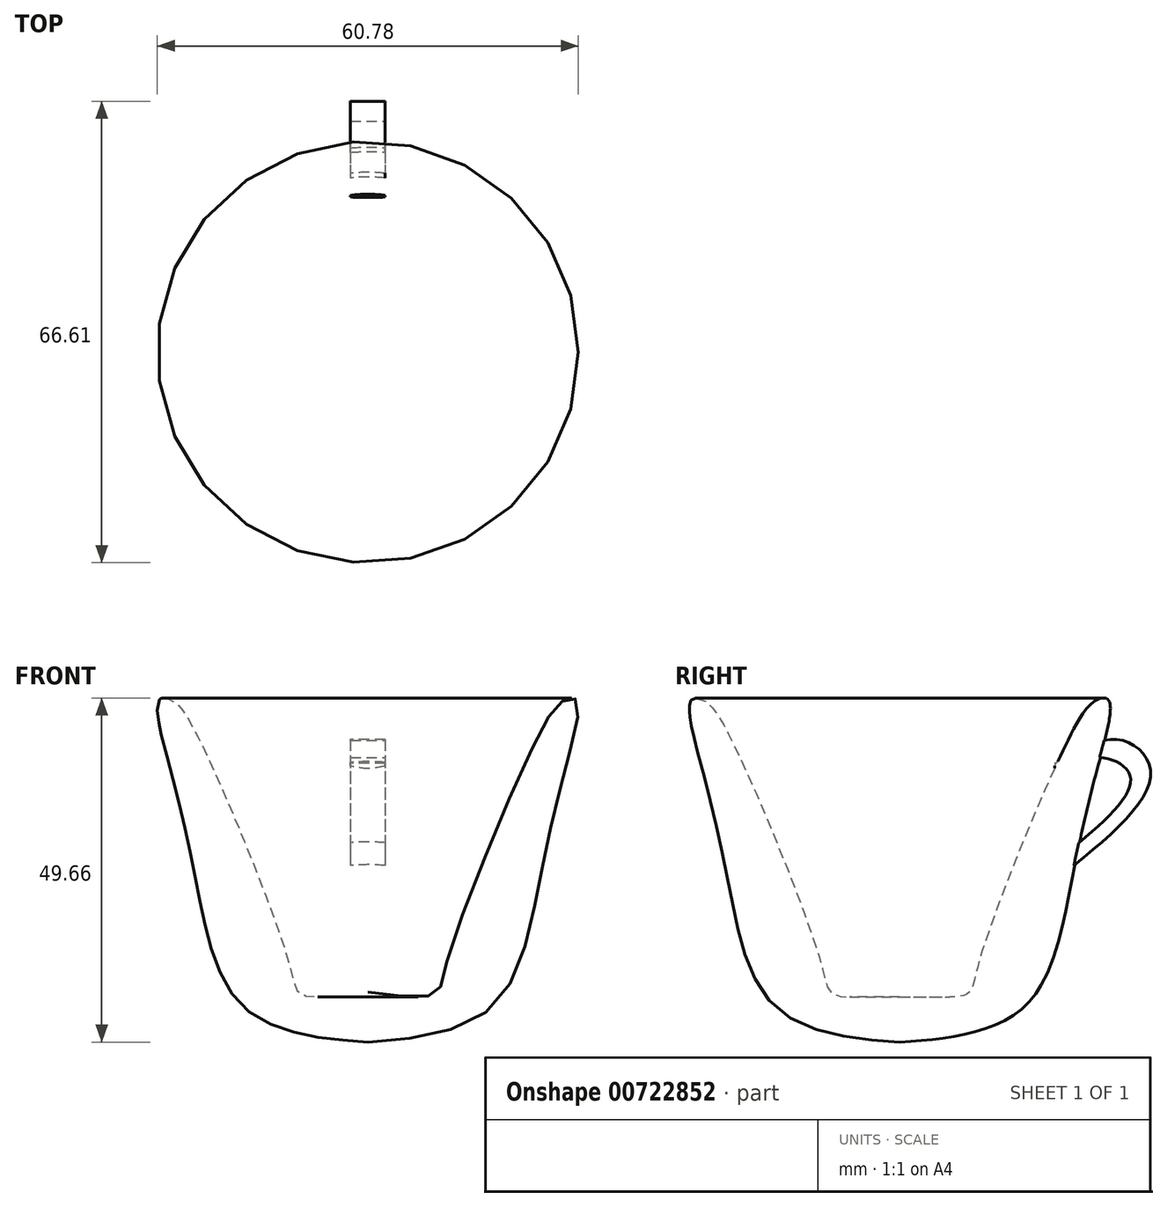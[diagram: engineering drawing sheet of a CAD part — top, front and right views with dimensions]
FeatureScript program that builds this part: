
annotation { "Feature Type Name" : "Feature", "Feature Type Description" : "" }
export const myFeature = defineFeature(function(context is Context, id is Id, definition is map)
    precondition{}
    {
        {
            var Q0;
            Q0=qCreatedBy(makeId("Front.planeOp"),FACE);
            var sketch = newSketch(context, id + "F0", { "sketchPlane" : qUnion([Q0])});
            skFitSpline(sketch, "E0", {"points": [v(0, -14.18) * mm, v(9.43, -14.6) * mm, v(11.27, -10.4) * mm, v(24.36, 22.32) * mm, v(28.48, 27.99) * mm, v(30.14, 27.9) * mm, v(28.24, 17.01) * mm, v(24.44, 0) * mm, v(17.76, -16.52) * mm, v(0, -21.42) * mm], "startDerivative": vector(110.62, -14.1) * mm, "endDerivative": vector(-134.6, -8.53) * mm});
            skLineSegment(sketch, "E1", {"start": v(0, -14.18) * mm, "end": v(0, -21.42) * mm});
            skSolve(sketch);
        }
        {
            var Q0;
            Q0 = qSketchRegion(id + "F0", true);
            var Q1;
            Q1=sQuery(id+"F0.wireOp",EDGE,"E1");
            revolve(context, id + "F1", {"surfaceOperationType" : NewSurfaceOperationType.NEW, "entities" : qUnion([Q0]), "axis" : qUnion([Q1]), "revolveType" : RevolveType.FULL});
        }
        {
            var Q0;
            Q0=qCreatedBy(makeId("Right.planeOp"),FACE);
            var sketch = newSketch(context, id + "F2", { "sketchPlane" : qUnion([Q0])});
            skFitSpline(sketch, "E2", {"points": [v(22.43, 18.84) * mm, v(31.95, 22.14) * mm, v(36.22, 17.1) * mm, v(22.24, 1.75) * mm], "startDerivative": vector(32.32, 18.87) * mm, "endDerivative": vector(-46.82, -37.2) * mm});
            skFitSpline(sketch, "E3", {"points": [v(22.24, 17.1) * mm, v(29.14, 19.63) * mm, v(33.32, 16.52) * mm, v(20.9, 3.46) * mm], "startDerivative": vector(23.21, 13.83) * mm, "endDerivative": vector(-41.38, -32.16) * mm});
            skLineSegment(sketch, "E4", {"start": v(22.43, 18.84) * mm, "end": v(22.24, 17.1) * mm});
            skLineSegment(sketch, "E5", {"start": v(22.24, 1.75) * mm, "end": v(20.9, 3.46) * mm});
            skSolve(sketch);
        }
        {
            var Q0;
            Q0 = qSketchRegion(id + "F2", true);
            extrude(context, id + "F3", {"entities" : qUnion([Q0]), "operationType" : NewBodyOperationType.ADD, "endBound" : BoundingType.SYMMETRIC, "depth" : 5 * mm, "offsetDistance" : 25 * mm});
        }
    });
